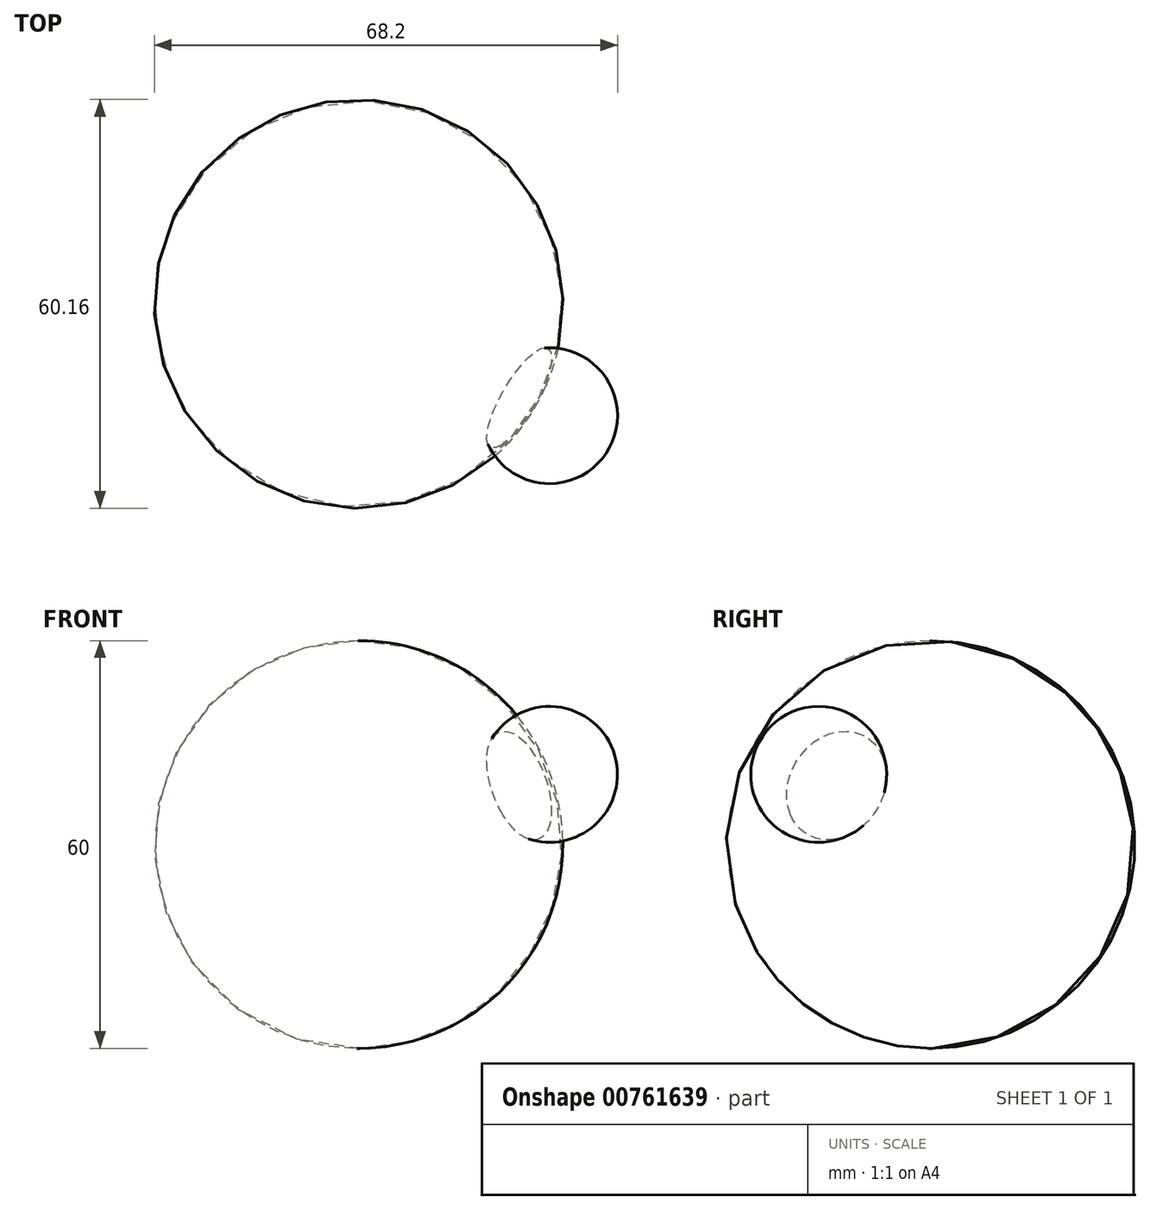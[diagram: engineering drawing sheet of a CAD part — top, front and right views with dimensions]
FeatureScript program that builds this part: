
annotation { "Feature Type Name" : "Feature", "Feature Type Description" : "" }
export const myFeature = defineFeature(function(context is Context, id is Id, definition is map)
    precondition{}
    {
        {
            var Q0;
            Q0=qCreatedBy(makeId("Front.planeOp"),FACE);
            var sketch = newSketch(context, id + "F0", { "sketchPlane" : qUnion([Q0])});
            skLineSegment(sketch, "E0", {"start": v(0, 0) * mm, "end": v(0, 60) * mm});
            skArc(sketch, "E1", {"start": v(0, 0) * mm, "mid": v(29.92, 30) * mm, "end": v(0, 60) * mm});
            skSolve(sketch);
        }
        {
            var Q0;
            Q0=qCreatedBy(makeId("Front.planeOp"),FACE);
            var sketch = newSketch(context, id + "F1", { "sketchPlane" : qUnion([Q0])});
            skLineSegment(sketch, "E2", {"start": v(0, 0) * mm, "end": v(0, 60.18) * mm, "construction": true});
            skLineSegment(sketch, "E3", {"start": v(0, 30.1) * mm, "end": v(28.12, 40.32) * mm, "construction": true});
            skSolve(sketch);
        }
        {
            var Q0;
            Q0=sQuery(id+"F1.wireOp",VERTEX,"E3.end");
            var Q1;
            Q1=sQuery(id+"F1.wireOp",EDGE,"E3");
            cPlane(context, id + "F2", {"entities" : qUnion([Q0, Q1]), "cplaneType" : CPlaneType.LINE_POINT, "offset" : 25 * mm, "width" : 150 * mm, "height" : 150 * mm});
        }
        {
            var Q0;
            Q0 = qSketchRegion(id + "F0", true);
            var Q1;
            Q1=sQuery(id+"F1.wireOp",EDGE,"E2");
            revolve(context, id + "F3", {"surfaceOperationType" : NewSurfaceOperationType.NEW, "entities" : qUnion([Q0]), "axis" : qUnion([Q1]), "revolveType" : RevolveType.FULL});
        }
        {
            var Q0;
            Q0=qCreatedBy(id+"F2.planeOp",FACE);
            var sketch = newSketch(context, id + "F4", { "sketchPlane" : qUnion([Q0])});
            skLineSegment(sketch, "E4", {"start": v(-26.45, 28.28) * mm, "end": v(-6.45, 28.28) * mm});
            skArc(sketch, "E5", {"start": v(-6.45, 28.28) * mm, "mid": v(-16.45, 38.28) * mm, "end": v(-26.45, 28.28) * mm});
            skSolve(sketch);
        }
        {
            var Q0;
            Q0 = qSketchRegion(id + "F4", true);
            var Q1;
            Q1=sQuery(id+"F4.wireOp",EDGE,"E4");
            revolve(context, id + "F5", {"operationType" : NewBodyOperationType.ADD, "surfaceOperationType" : NewSurfaceOperationType.NEW, "entities" : qUnion([Q0]), "axis" : qUnion([Q1]), "revolveType" : RevolveType.FULL});
        }
    });
